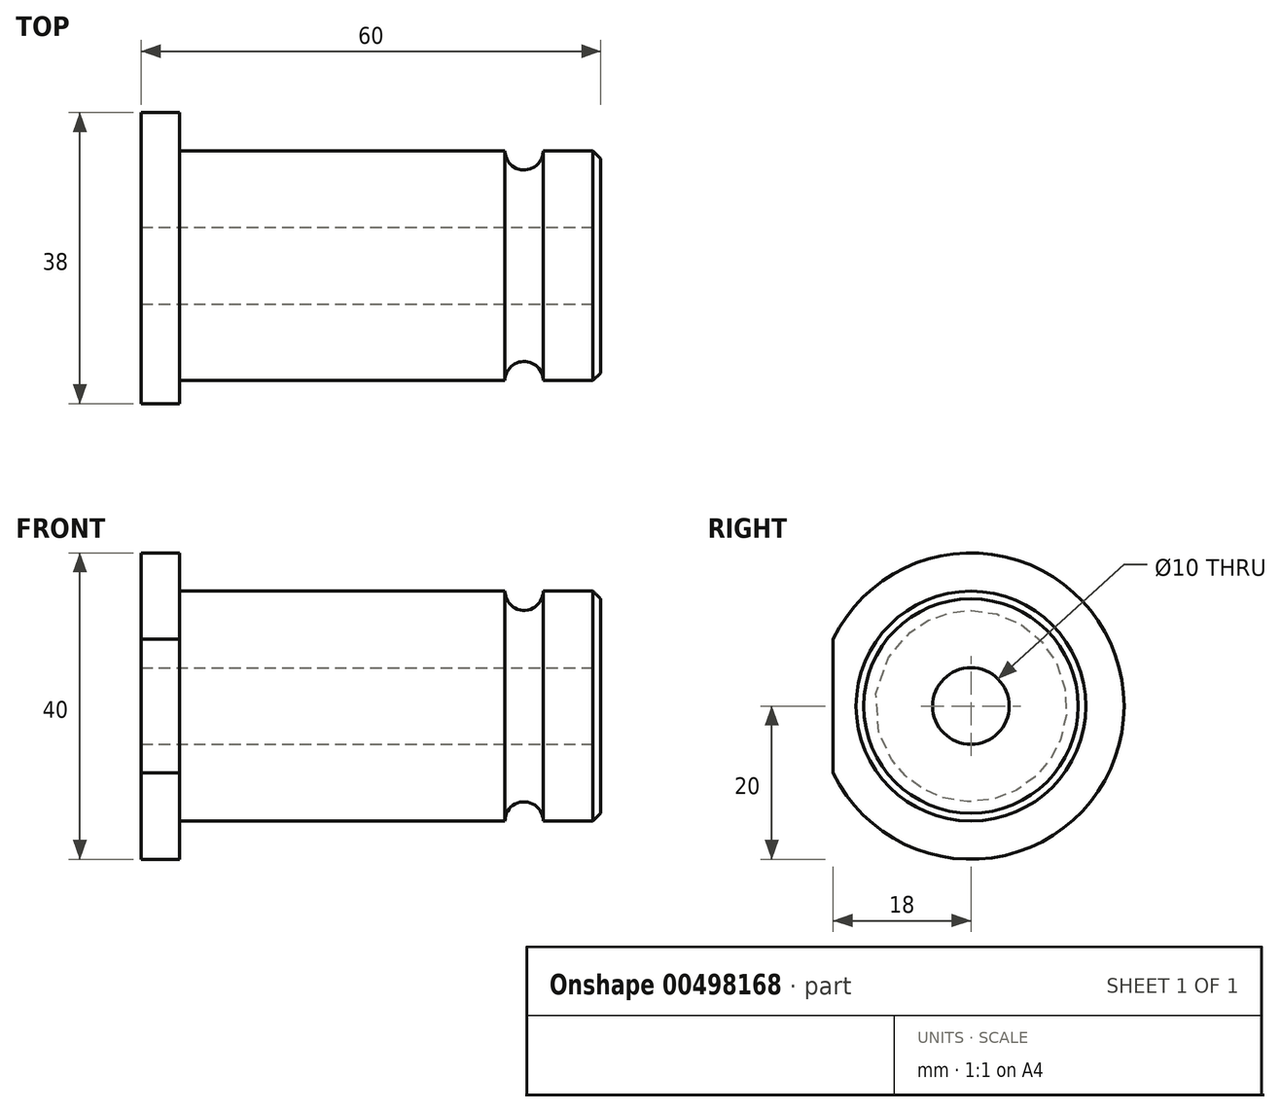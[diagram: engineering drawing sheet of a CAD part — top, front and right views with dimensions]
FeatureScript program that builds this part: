
annotation { "Feature Type Name" : "Feature", "Feature Type Description" : "" }
export const myFeature = defineFeature(function(context is Context, id is Id, definition is map)
    precondition{}
    {
        {
            var Q0;
            Q0=qCreatedBy(makeId("Front.planeOp"),FACE);
            var sketch = newSketch(context, id + "F0", { "sketchPlane" : qUnion([Q0])});
            skLineSegment(sketch, "E0", {"start": v(0, 0) * mm, "end": v(0, 20) * mm});
            skLineSegment(sketch, "E1", {"start": v(0, 20) * mm, "end": v(5, 20) * mm});
            skLineSegment(sketch, "E2", {"start": v(5, 20) * mm, "end": v(5, 15) * mm});
            skLineSegment(sketch, "E3", {"start": v(5, 15) * mm, "end": v(60, 15) * mm});
            skLineSegment(sketch, "E4", {"start": v(60, 15) * mm, "end": v(60, 0) * mm});
            skLineSegment(sketch, "E5", {"start": v(60, 0) * mm, "end": v(0, 0) * mm});
            skLineSegment(sketch, "E6", {"start": v(69.86, 0) * mm, "end": v(-7.51, 0) * mm, "construction": true});
            skSolve(sketch);
        }
        {
            var Q0;
            Q0=qSketchRegion(id+"F0",true);
            var Q1;
            Q1=sQuery(id+"F0.wireOp",EDGE,"E6");
            revolve(context, id + "F1", {"entities" : qUnion([Q0]), "axis" : qUnion([Q1]), "revolveType" : RevolveType.FULL});
        }
        {
            var Q0;
            Q0=makeQuery(id+"F1.opRevolve","SWEPT_FACE",FACE,{"disambiguationData":[OSD([sQuery(id+"F0.wireOp",EDGE,"E4")])]});
            var sketch = newSketch(context, id + "F2", { "sketchPlane" : qUnion([Q0])});
            skCircle(sketch, "E7", {"center": v(0, 0) * mm, "radius": 5 * mm});
            skSolve(sketch);
        }
        {
            var Q0;
            Q0=qSketchRegion(id+"F2",true);
            extrude(context, id + "F3", {"entities" : qUnion([Q0]), "operationType" : NewBodyOperationType.REMOVE, "endBound" : BoundingType.THROUGH_ALL, "oppositeDirection" : true, "depth" : 25 * mm});
        }
        {
            var Q0;
            Q0=makeQuery(id+"F1.opRevolve","SWEPT_EDGE",EDGE,{"disambiguationData":[OSD([sQuery(id+"F0.wireOp",EDGE,"E3"),sQuery(id+"F0.wireOp",EDGE,"E4")])]});
            chamfer(context, id + "F4", {"entities" : qUnion([Q0]), "width" : 1 * mm, "tangentPropagation" : true});
        }
        {
            var Q0;
            Q0=qCreatedBy(makeId("Front.planeOp"),FACE);
            var sketch = newSketch(context, id + "F5", { "sketchPlane" : qUnion([Q0])});
            skCircle(sketch, "E8", {"center": v(50, 15) * mm, "radius": 2.5 * mm});
            skSolve(sketch);
        }
        {
            var Q0;
            Q0=qSketchRegion(id+"F5",true);
            var Q1;
            Q1=sQuery(id+"F0.wireOp",EDGE,"E6");
            revolve(context, id + "F6", {"operationType" : NewBodyOperationType.REMOVE, "entities" : qUnion([Q0]), "axis" : qUnion([Q1]), "revolveType" : RevolveType.FULL, "oppositeDirection" : true});
        }
        {
            var Q0;
            Q0=makeQuery(id+"F1.opRevolve","SWEPT_FACE",FACE,{"disambiguationData":[OSD([sQuery(id+"F0.wireOp",EDGE,"E0")])]});
            var sketch = newSketch(context, id + "F7", { "sketchPlane" : qUnion([Q0])});
            skCircle(sketch, "E9", {"center": v(0, 0) * mm, "radius": 20 * mm});
            skLineSegment(sketch, "E10", {"start": v(18, 8.72) * mm, "end": v(18, -8.72) * mm});
            skLineSegment(sketch, "E11", {"start": v(0, 27.13) * mm, "end": v(0, -24.3) * mm, "construction": true});
            skSolve(sketch);
        }
        {
            var Q0;
            Q0=makeQuery(id+"F7.imprint","IMPRINT",FACE,{"disambiguationData":[TD([[makeQuery(id+"F7.imprint","IMPRINT",EDGE,{"derivedFrom":makeQuery(id+"F3.boolean.opBoolean","INTERSECT",EDGE,{"derivedFrom":[makeQuery(id+"F1.opRevolve","SWEPT_FACE",FACE,{"disambiguationData":[OSD([sQuery(id+"F0.wireOp",EDGE,"E0")])]}),makeQuery(id+"F3.opExtrude","SWEPT_FACE",FACE,{"disambiguationData":[OSD([sQuery(id+"F2.wireOp",EDGE,"E7")])]})]})}),-1.0]])]});
            var Q1;
            {var subQ0=sQuery(id+"F7.wireOp",EDGE,"E10");Q1=makeQuery(id+"F7.imprint","IMPRINT",FACE,{"disambiguationData":[TD([[makeQuery(id+"F7.imprint","IMPRINT",EDGE,{"derivedFrom":subQ0}),1.0]])]});}
            var Q2;
            Q2=makeQuery(id+"F1.opRevolve","SWEPT_FACE",FACE,{"disambiguationData":[OSD([sQuery(id+"F0.wireOp",EDGE,"E2")])]});
            extrude(context, id + "F8", {"entities" : qUnion([Q0, Q1]), "operationType" : NewBodyOperationType.REMOVE, "endBound" : BoundingType.UP_TO_SURFACE, "oppositeDirection" : true, "endBoundEntityFace" : qUnion([Q2]), "depth" : 25 * mm});
        }
    });
